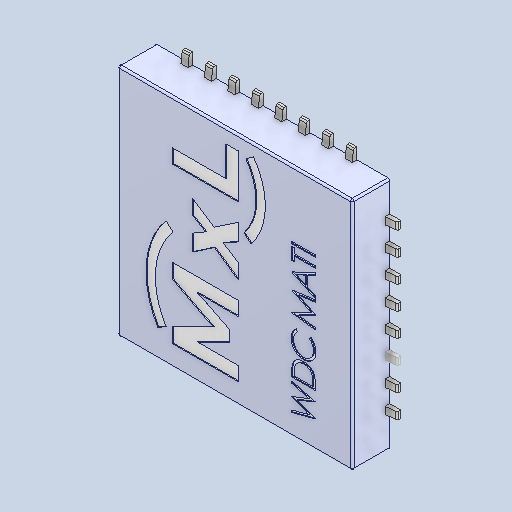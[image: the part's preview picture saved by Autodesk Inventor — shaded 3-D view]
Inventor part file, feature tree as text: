
AUTODESK INVENTOR PART (.ipt)
format: ipt  version: 2022 (Build 260153000, 153)  size: 431,104 bytes
history: mixed  units: in
note: dims shown in document units (in); Inventor stores cm internally (conversion verified against a paired STEP export)
features: other x33, fillet x1, imported_body x1
ambient origin geometry x8: Origin, YZ Plane, XZ Plane, XY Plane, X Axis, Y Axis, Z Axis, Center Point
bodies: Solid1 (imported_parasolid), Solid2 (imported_parasolid), Solid3 (imported_parasolid), Solid4 (imported_parasolid), Solid5 (imported_parasolid), Solid6 (imported_parasolid), Solid7 (imported_parasolid), Solid8 (imported_parasolid), Solid9 (imported_parasolid), Solid10 (imported_parasolid), Solid11 (imported_parasolid), Solid12 (imported_parasolid), Solid13 (imported_parasolid), Solid14 (imported_parasolid), Solid15 (imported_parasolid), Solid16 (imported_parasolid), Solid17 (imported_parasolid), Solid18 (imported_parasolid), Solid19 (imported_parasolid), Solid20 (imported_parasolid), Solid21 (imported_parasolid), Solid22 (imported_parasolid), Solid23 (imported_parasolid), Solid24 (imported_parasolid), Solid25 (imported_parasolid), Solid26 (imported_parasolid), Solid27 (imported_parasolid), Solid28 (imported_parasolid), Solid29 (imported_parasolid), Solid30 (imported_parasolid), Solid31 (imported_parasolid), Solid32 (imported_parasolid), Solid33 (imported_parasolid), Solid34 (imported_parasolid)
feature tree (35):
  other  "Cut-Extrude2"
  other  "LPattern1[1]"
  other  "LPattern1[2]"
  other  "LPattern1[3]"
  other  "LPattern1[4]"
  other  "LPattern1[5]"
  other  "LPattern1[6]"
  other  "LPattern1[7]"
  other  "Boss-Extrude3"
  other  "CirPattern1[1]"
  other  "CirPattern1[2]"
  other  "CirPattern1[3]"
  other  "CirPattern1[4]"
  other  "CirPattern1[5]"
  other  "CirPattern1[6]"
  other  "CirPattern1[7]"
  other  "CirPattern1[8]"
  other  "CirPattern1[9]"
  other  "CirPattern1[10]"
  other  "CirPattern1[11]"
  other  "CirPattern1[12]"
  other  "CirPattern1[13]"
  other  "CirPattern1[14]"
  other  "CirPattern1[15]"
  other  "CirPattern1[16]"
  other  "CirPattern1[17]"
  other  "CirPattern1[18]"
  other  "CirPattern1[19]"
  other  "CirPattern1[20]"
  other  "CirPattern1[21]"
  other  "CirPattern1[22]"
  other  "CirPattern1[23]"
  other  "CirPattern1[24]"
  fillet  "Fillet4"  [1 undecoded]
  imported_body  NMx_Import_Brep_tag  [imported B-rep: ~242 faces, bbox_mm=[5.48, 5.48, 0.9]]
note: 1 required parameter value undecoded (feature->parameter linkage not recoverable at this tier; creation-order binding heuristic only, values carry confidence <= 0.55)
